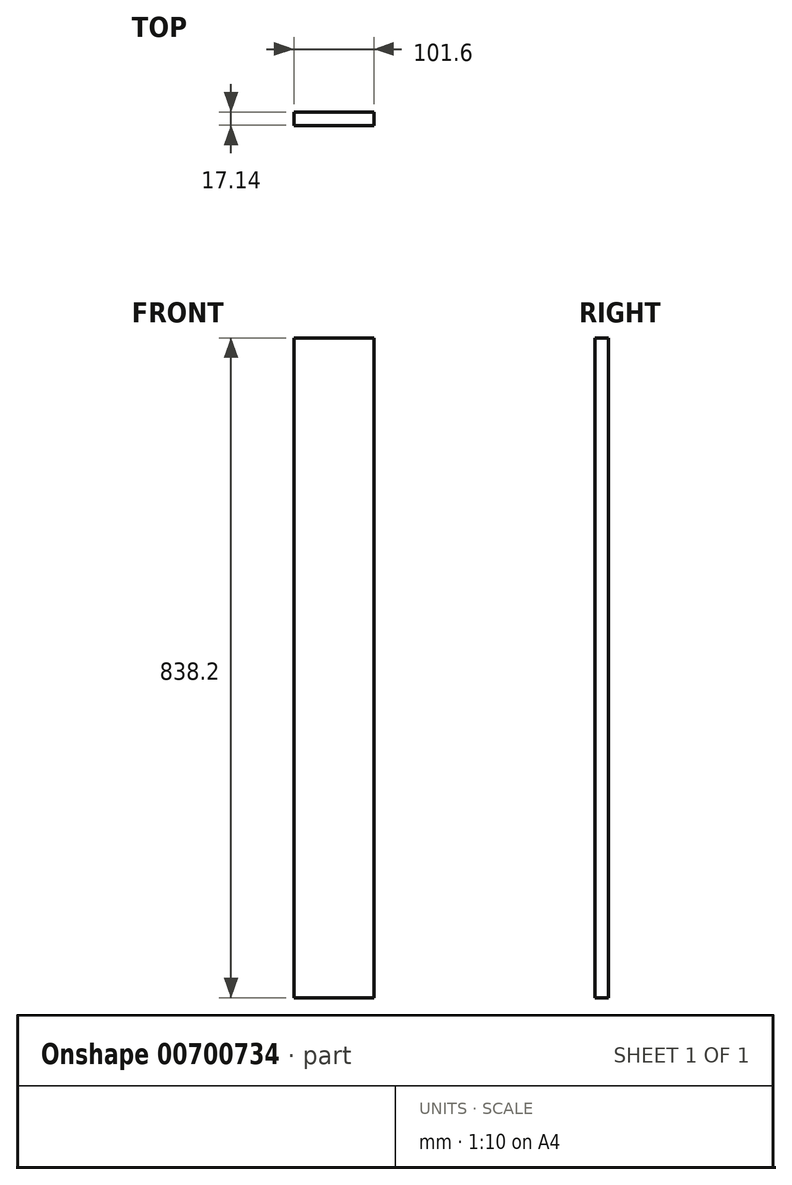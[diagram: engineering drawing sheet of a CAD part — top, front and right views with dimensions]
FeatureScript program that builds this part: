
annotation { "Feature Type Name" : "Feature", "Feature Type Description" : "" }
export const myFeature = defineFeature(function(context is Context, id is Id, definition is map)
    precondition{}
    {
        {
            var Q0;
            Q0=qCreatedBy(makeId("Front.planeOp"),FACE);
            var sketch = newSketch(context, id + "F0", { "sketchPlane" : qUnion([Q0])});
            skLineSegment(sketch, "E0.bottom", {"start": v(0, 0) * mm, "end": v(101.6, 0) * mm});
            skLineSegment(sketch, "E0.top", {"start": v(0, 838.2) * mm, "end": v(101.6, 838.2) * mm});
            skLineSegment(sketch, "E0.left", {"start": v(0, 0) * mm, "end": v(0, 838.2) * mm});
            skLineSegment(sketch, "E0.right", {"start": v(101.6, 0) * mm, "end": v(101.6, 838.2) * mm});
            skSolve(sketch);
        }
        {
            var Q0;
            Q0 = qSketchRegion(id + "F0", true);
            extrude(context, id + "F1", {"entities" : qUnion([Q0]), "depth" : 17.14 * mm, "offsetDistance" : 25.4 * mm});
        }
    });
